# Revit family: ReCool_Line_05_iK
name_source: partatom
category: HLS-Bauteile
units: mm (PartAtom-declared; Revit-internal decimal feet)

## family parameters
Arbeitsebenenbasiert = Nein
Beim Laden mit Abzugskörper schneiden = Nein
Bemaßung runder Anschluss = Durchmesser verwenden
Gemeinsam genutzt = Nein
Immer vertikal = Ja
Klassifizierung = Keine
Raumberechnungspunkt = Nein
Teiletyp = Normal

## types (1)
- ReCool_Line_05_iK
    Bauelement = 29.02.01.01
    Beschreibung = RLT-Gerät
    Classification.OmniClass.23.Description = Pre Fabricated Air Handling Units
    Classification.OmniClass.23.Number = 23-33 25 19
    Family.Subcategory.Name = Air Handling Unit
    Hersteller = Hansa
    Modell = ReCool-Line-05-iK
    RLT_Breite = 880 mm  [stored 2.88714 ft]
    RLT_Grundrahmen = 635 mm
    RLT_Höhe = 1950 mm  [stored 6.39764 ft]
    RLT_Kälte_Anschluss_AUS = 18 mm
    RLT_Kälte_Anschluss_EIN = 22 mm
    RLT_Länge = 1350 mm  [stored 4.42913 ft]
    RLT_Volumenstrom_max = 5000 m³/h
    Vorgabe-Ansicht = 0 mm  [stored 0 ft]

note: [stored X ft] marks values corroborated as IEEE doubles in the binary element streams (Revit-internal decimal feet)

## geometry (parser evidence)
native form markers: Sweep x3
no freeform markers — native parametric forms only
